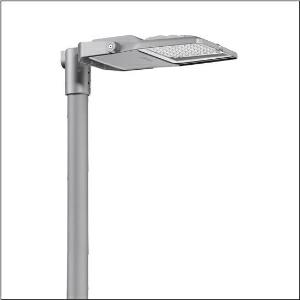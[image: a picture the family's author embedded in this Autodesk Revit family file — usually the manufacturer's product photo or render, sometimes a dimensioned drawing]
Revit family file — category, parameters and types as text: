
# Revit family: floodlight_fl_21_mini___pl33t_5xa7776d2f3a_276e
name_source: partatom
category: Lighting Fixtures
units: mm (PartAtom-declared; Revit-internal decimal feet)

## family parameters
Cut with Voids When Loaded = No
Host = Face
Light Source = No
Part Type = Normal
Room Calculation Point = No
Round Connector Dimension = Use Diameter
Shared = No

## types (1)
- --- (1 x LED, 17630 lm, 142.9 W, 3000K)
    Apparent Load = 143 VA
    CIE Flux Codes = 26 75 99 100 100
    Color Rendering = 70
    Color Temperature = 3000K
    Default Elevation = 1800 mm
    Description = Floodlight FL 21 mini, floodlight, primary light control with lens, of PMMA, primary optical cover: protective disc, of toughened safety glass, transparent, light distribution: PL33T, light emission: direct distribution, installation type: surface-mounted, LED, High Power LED, rated luminous flux: 17.630lm, luminous efficacy: 123lm/W, light colour: 730, colour temperature: 3000K, control: flexible luminous flux parameterisation, time-dependent luminous flux control, constant luminous flux control, overheat protection, presetting dimming logarithmic, with terminal, 6-pole, mains connection: 220..240V, AC, 50/60Hz, start of lifetime: 143W, end of service life: 151W, reduction: 63W, luminaire housing, of diecast aluminium, powder-coated, Siteco® metallic grey (DB 702S), corrosivity category C5 mid according to DIN EN ISO 12944, sealing non-destructively replaceable, please order mast flange separately, mast bracket, of steel, galvanised, powder-coated, Siteco® metallic grey (DB 702S), Smart Interface below and above, protection rating (complete): IP66, insulation class (complete): insulation class II (safety insulation), certification: CE, ENEC, VDE, protection symbol: D, impact resistance: IK08, permissible operating ambient temperature: -40..+40°C, permissible operating ambient temperature for outdoor applications: -40..+50°C, standard: DIN EN 12944, LABS conformity tested according to VDMA 24364:2018-05, packaging unit: 1 piece

Light Distribution: PL33T
    Height = 70 mm
    Lamp = 1 x LED
    Lamp Light Flux = 17630 lm
    Lamp Power = 142.9 W
    Lamp count = 1
    Length = 485 mm
    Luminous efficacy = 123 lm/W
    Manufacturer = Siteco
    ModVariant = No
    Model = 5XA7776D2F3A
    Number of Poles = 1
    OnlyDefault = Yes
    Power Factor = 1
    Product Name = Floodlight FL 21 mini | PL33T
    Product group = floodlight | pylon annexe
    ProductGroupID = 6200
    Protection Class = Protection class II
    Protection Degree = IP 66
    RLX_Detail_Level = 1
    RLX_Emergency_Light_Flux = 0 lm
    RLX_Emergency_Type = 0
    RLX_Emergency_Type_DB = No
    RlxData = <blob elided: 101209 chars, md5=d0bc0d5f>
    Socket = socket
    Standby Power = 0 W
    System Light Flux = 17630 lm
    System Power = 143 W
    Type Comments = factory setting: luminous flux: 100 % | dim-lin: 254 | 730 mA
    Type Image = l_1007125.jpg
    URL = http://relux.com
    VarID = @adj_098491
    Voltage = 0 V
    Weight = 0.00 kg
    Width = 337 mm

## geometry (parser evidence)
native form markers: Blend x4, Sweep x10
no freeform markers — native parametric forms only
